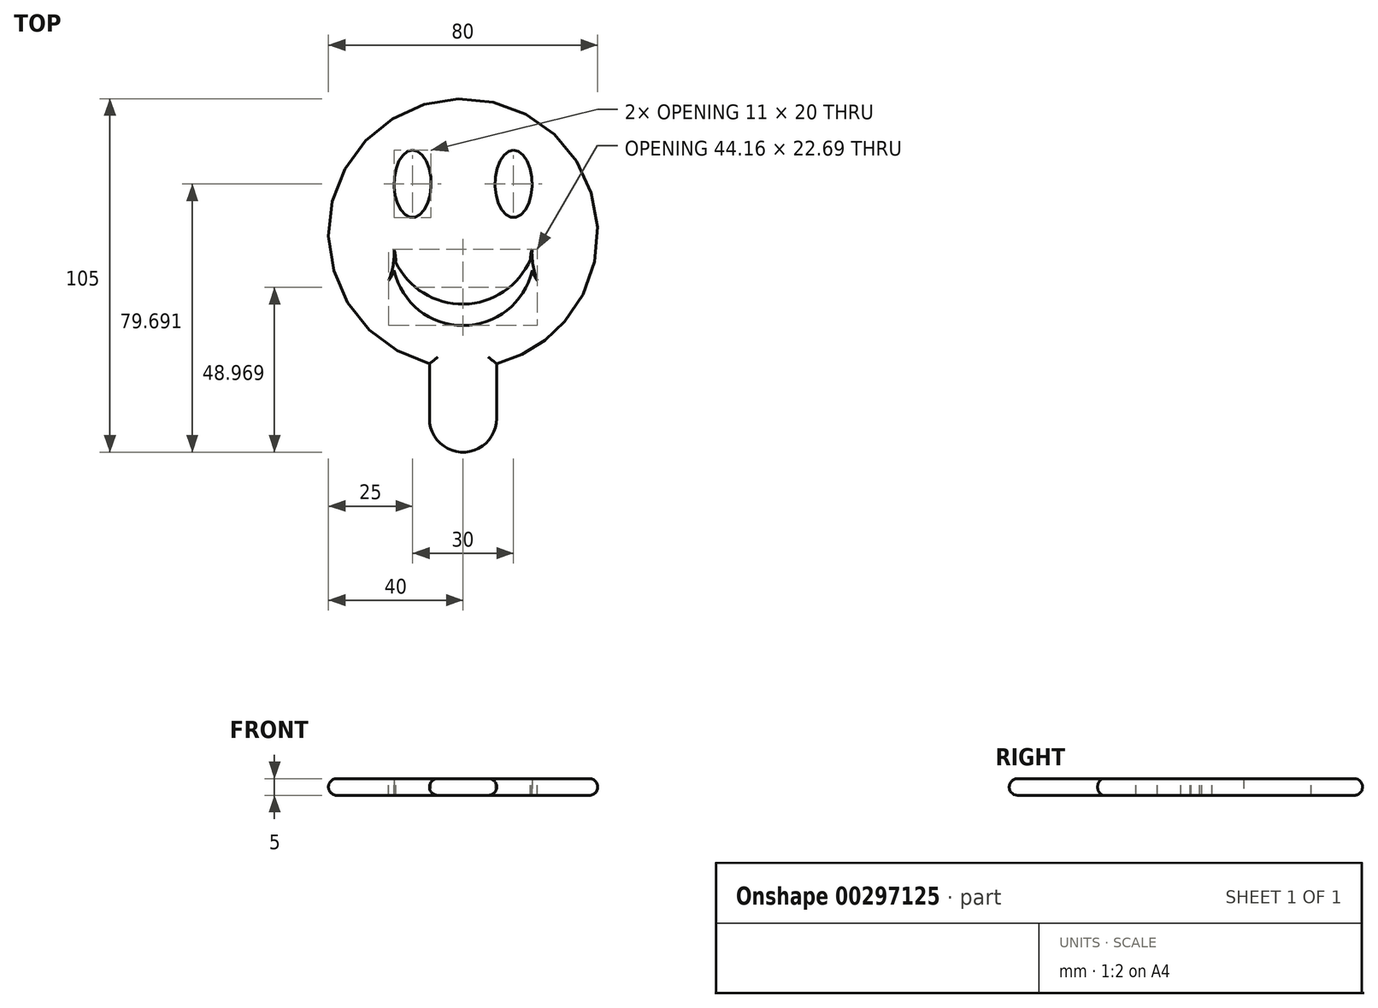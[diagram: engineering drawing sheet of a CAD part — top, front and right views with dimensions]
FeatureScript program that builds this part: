
annotation { "Feature Type Name" : "Feature", "Feature Type Description" : "" }
export const myFeature = defineFeature(function(context is Context, id is Id, definition is map)
    precondition{}
    {
        {
            var Q0;
            Q0=qCreatedBy(makeId("Top.planeOp"),FACE);
            var sketch = newSketch(context, id + "F0", { "sketchPlane" : qUnion([Q0])});
            skCircle(sketch, "E0", {"center": v(0, 0) * mm, "radius": 40 * mm});
            skText(sketch, "E1", { "text": "JODIE", "fontName": "AllertaStencil-Regular.ttf"});
            const initialGuessF0  = {"E1": [-0.0273, -0.00648, 1, 0, 0.0135]};
            skSetInitialGuess(sketch, initialGuessF0);
            skSolve(sketch);
        }
        {
            var Q0;
            Q0=qSketchRegion(id+"F0",true);
            extrude(context, id + "F1", {"entities" : qUnion([Q0]), "depth" : 5 * mm});
        }
        {
            var Q0;
            Q0=qCreatedBy(makeId("Top.planeOp"),FACE);
            var sketch = newSketch(context, id + "F2", { "sketchPlane" : qUnion([Q0])});
            skLineSegment(sketch, "E2.bottom", {"start": v(-10, -65) * mm, "end": v(10, -65) * mm});
            skLineSegment(sketch, "E2.top", {"start": v(-10, 65) * mm, "end": v(10, 65) * mm});
            skLineSegment(sketch, "E2.left", {"start": v(-10, -65) * mm, "end": v(-10, 65) * mm});
            skLineSegment(sketch, "E2.right", {"start": v(10, -65) * mm, "end": v(10, 65) * mm});
            skPoint(sketch, "E2.middle", {"position": v(0, 0) * mm});
            skLineSegment(sketch, "E3", {"start": v(-10, -31.18) * mm, "end": v(10, -31.18) * mm});
            skSolve(sketch);
        }
        {
            var Q0;
            {var subQ0=sQuery(id+"F2.wireOp",EDGE,"E2.bottom");Q0=makeQuery(id+"F2.imprint","IMPRINT",FACE,{"disambiguationData":[TD([[makeQuery(id+"F2.imprint","IMPRINT",EDGE,{"derivedFrom":subQ0}),1.0]])]});}
            extrude(context, id + "F3", {"entities" : qUnion([Q0]), "operationType" : NewBodyOperationType.ADD, "depth" : 5 * mm});
        }
        {
            var Q0;
            Q0=makeQuery(id+"F3.opExtrude","SWEPT_EDGE",EDGE,{"disambiguationData":[OSD([sQuery(id+"F2.wireOp",EDGE,"E2.bottom"),sQuery(id+"F2.wireOp",EDGE,"E2.left")])]});
            var Q1;
            Q1=makeQuery(id+"F3.opExtrude","SWEPT_EDGE",EDGE,{"disambiguationData":[OSD([sQuery(id+"F2.wireOp",EDGE,"E2.bottom"),sQuery(id+"F2.wireOp",EDGE,"E2.right")])]});
            fillet(context, id + "F4", {"entities" : qUnion([Q0, Q1]), "radius" : 10 * mm, "tangentPropagation" : true, "allowEdgeOverflow" : false});
        }
        {
            var Q0;
            Q0=makeQuery(id+"F1.opExtrude","CAP_EDGE",EDGE,{"disambiguationData":[OSD([sQuery(id+"F0.wireOp",EDGE,"E0")])],"isStart":false});
            var Q1;
            Q1=makeQuery(id+"F3.opExtrude","CAP_EDGE",EDGE,{"disambiguationData":[OSD([sQuery(id+"F2.wireOp",EDGE,"E2.left")])],"isStart":false});
            fillet(context, id + "F5", {"entities" : qUnion([Q0, Q1]), "radius" : 2.5 * mm, "tangentPropagation" : true, "allowEdgeOverflow" : false});
        }
        {
            var Q0;
            Q0=makeQuery(id+"F1.opExtrude","CAP_EDGE",EDGE,{"disambiguationData":[OSD([sQuery(id+"F0.wireOp",EDGE,"E0")])],"isStart":true});
            var Q1;
            Q1=makeQuery(id+"F3.opExtrude","CAP_EDGE",EDGE,{"disambiguationData":[OSD([sQuery(id+"F2.wireOp",EDGE,"E2.left")])],"isStart":true});
            fillet(context, id + "F6", {"entities" : qUnion([Q0, Q1]), "radius" : 2.5 * mm, "tangentPropagation" : true, "allowEdgeOverflow" : false});
        }
        {
            var Q0;
            Q0=makeQuery(id+"F3.boolean.opBoolean","MERGE",FACE,{"derivedFrom":[makeQuery(id+"F1.opExtrude","CAP_FACE",FACE,{"disambiguationData":[OSD([sQuery(id+"F0.wireOp",EDGE,"E0"),sQuery(id+"F0.wireOp",EDGE,"E1.sketch_text.stroke-0"),sQuery(id+"F0.wireOp",EDGE,"E1.sketch_text.stroke-1"),sQuery(id+"F0.wireOp",EDGE,"E1.sketch_text.stroke-2"),sQuery(id+"F0.wireOp",EDGE,"E1.sketch_text.stroke-3"),sQuery(id+"F0.wireOp",EDGE,"E1.sketch_text.stroke-4"),sQuery(id+"F0.wireOp",EDGE,"E1.sketch_text.stroke-5"),sQuery(id+"F0.wireOp",EDGE,"E1.sketch_text.stroke-6"),sQuery(id+"F0.wireOp",EDGE,"E1.sketch_text.stroke-7"),sQuery(id+"F0.wireOp",EDGE,"E1.sketch_text.stroke-8"),sQuery(id+"F0.wireOp",EDGE,"E1.sketch_text.stroke-9"),sQuery(id+"F0.wireOp",EDGE,"E1.sketch_text.stroke-10"),sQuery(id+"F0.wireOp",EDGE,"E1.sketch_text.stroke-11"),sQuery(id+"F0.wireOp",EDGE,"E1.sketch_text.stroke-12"),sQuery(id+"F0.wireOp",EDGE,"E1.sketch_text.stroke-13"),sQuery(id+"F0.wireOp",EDGE,"E1.sketch_text.stroke-14"),sQuery(id+"F0.wireOp",EDGE,"E1.sketch_text.stroke-15"),sQuery(id+"F0.wireOp",EDGE,"E1.sketch_text.stroke-16"),sQuery(id+"F0.wireOp",EDGE,"E1.sketch_text.stroke-17"),sQuery(id+"F0.wireOp",EDGE,"E1.sketch_text.stroke-18"),sQuery(id+"F0.wireOp",EDGE,"E1.sketch_text.stroke-19"),sQuery(id+"F0.wireOp",EDGE,"E1.sketch_text.stroke-20"),sQuery(id+"F0.wireOp",EDGE,"E1.sketch_text.stroke-21"),sQuery(id+"F0.wireOp",EDGE,"E1.sketch_text.stroke-22"),sQuery(id+"F0.wireOp",EDGE,"E1.sketch_text.stroke-23"),sQuery(id+"F0.wireOp",EDGE,"E1.sketch_text.stroke-24"),sQuery(id+"F0.wireOp",EDGE,"E1.sketch_text.stroke-25"),sQuery(id+"F0.wireOp",EDGE,"E1.sketch_text.stroke-26"),sQuery(id+"F0.wireOp",EDGE,"E1.sketch_text.stroke-27"),sQuery(id+"F0.wireOp",EDGE,"E1.sketch_text.stroke-28"),sQuery(id+"F0.wireOp",EDGE,"E1.sketch_text.stroke-29"),sQuery(id+"F0.wireOp",EDGE,"E1.sketch_text.stroke-30"),sQuery(id+"F0.wireOp",EDGE,"E1.sketch_text.stroke-31"),sQuery(id+"F0.wireOp",EDGE,"E1.sketch_text.stroke-32"),sQuery(id+"F0.wireOp",EDGE,"E1.sketch_text.stroke-33"),sQuery(id+"F0.wireOp",EDGE,"E1.sketch_text.stroke-34"),sQuery(id+"F0.wireOp",EDGE,"E1.sketch_text.stroke-35"),sQuery(id+"F0.wireOp",EDGE,"E1.sketch_text.stroke-36"),sQuery(id+"F0.wireOp",EDGE,"E1.sketch_text.stroke-37"),sQuery(id+"F0.wireOp",EDGE,"E1.sketch_text.stroke-38"),sQuery(id+"F0.wireOp",EDGE,"E1.sketch_text.stroke-39"),sQuery(id+"F0.wireOp",EDGE,"E1.sketch_text.stroke-40"),sQuery(id+"F0.wireOp",EDGE,"E1.sketch_text.stroke-41"),sQuery(id+"F0.wireOp",EDGE,"E1.sketch_text.stroke-42"),sQuery(id+"F0.wireOp",EDGE,"E1.sketch_text.stroke-43"),sQuery(id+"F0.wireOp",EDGE,"E1.sketch_text.stroke-44"),sQuery(id+"F0.wireOp",EDGE,"E1.sketch_text.stroke-45"),sQuery(id+"F0.wireOp",EDGE,"E1.sketch_text.stroke-46"),sQuery(id+"F0.wireOp",EDGE,"E1.sketch_text.stroke-47"),sQuery(id+"F0.wireOp",EDGE,"E1.sketch_text.stroke-48"),sQuery(id+"F0.wireOp",EDGE,"E1.sketch_text.stroke-49"),sQuery(id+"F0.wireOp",EDGE,"E1.sketch_text.stroke-50"),sQuery(id+"F0.wireOp",EDGE,"E1.sketch_text.stroke-51"),sQuery(id+"F0.wireOp",EDGE,"E1.sketch_text.stroke-52"),sQuery(id+"F0.wireOp",EDGE,"E1.sketch_text.stroke-53"),sQuery(id+"F0.wireOp",EDGE,"E1.sketch_text.stroke-54"),sQuery(id+"F0.wireOp",EDGE,"E1.sketch_text.stroke-55"),sQuery(id+"F0.wireOp",EDGE,"E1.sketch_text.stroke-56"),sQuery(id+"F0.wireOp",EDGE,"E1.sketch_text.stroke-57"),sQuery(id+"F0.wireOp",EDGE,"E1.sketch_text.stroke-58"),sQuery(id+"F0.wireOp",EDGE,"E1.sketch_text.stroke-59"),sQuery(id+"F0.wireOp",EDGE,"E1.sketch_text.stroke-60"),sQuery(id+"F0.wireOp",EDGE,"E1.sketch_text.stroke-61"),sQuery(id+"F0.wireOp",EDGE,"E1.sketch_text.stroke-62"),sQuery(id+"F0.wireOp",EDGE,"E1.sketch_text.stroke-63"),sQuery(id+"F0.wireOp",EDGE,"E1.sketch_text.stroke-64"),sQuery(id+"F0.wireOp",EDGE,"E1.sketch_text.stroke-65"),sQuery(id+"F0.wireOp",EDGE,"E1.sketch_text.stroke-66"),sQuery(id+"F0.wireOp",EDGE,"E1.sketch_text.stroke-67"),sQuery(id+"F0.wireOp",EDGE,"E1.sketch_text.stroke-68"),sQuery(id+"F0.wireOp",EDGE,"E1.sketch_text.stroke-69"),sQuery(id+"F0.wireOp",EDGE,"E1.sketch_text.stroke-70"),sQuery(id+"F0.wireOp",EDGE,"E1.sketch_text.stroke-71"),sQuery(id+"F0.wireOp",EDGE,"E1.sketch_text.stroke-72"),sQuery(id+"F0.wireOp",EDGE,"E1.sketch_text.stroke-73"),sQuery(id+"F0.wireOp",EDGE,"E1.sketch_text.stroke-74"),sQuery(id+"F0.wireOp",EDGE,"E1.sketch_text.stroke-75"),sQuery(id+"F0.wireOp",EDGE,"E1.sketch_text.stroke-76"),sQuery(id+"F0.wireOp",EDGE,"E1.sketch_text.stroke-77"),sQuery(id+"F0.wireOp",EDGE,"E1.sketch_text.stroke-78"),sQuery(id+"F0.wireOp",EDGE,"E1.sketch_text.stroke-79"),sQuery(id+"F0.wireOp",EDGE,"E1.sketch_text.stroke-80"),sQuery(id+"F0.wireOp",EDGE,"E1.sketch_text.stroke-81"),sQuery(id+"F0.wireOp",EDGE,"E1.sketch_text.stroke-82"),sQuery(id+"F0.wireOp",EDGE,"E1.sketch_text.stroke-83"),sQuery(id+"F0.wireOp",EDGE,"E1.sketch_text.stroke-84"),sQuery(id+"F0.wireOp",EDGE,"E1.sketch_text.stroke-85"),sQuery(id+"F0.wireOp",EDGE,"E1.sketch_text.stroke-86"),sQuery(id+"F0.wireOp",EDGE,"E1.sketch_text.stroke-87"),sQuery(id+"F0.wireOp",EDGE,"E1.sketch_text.stroke-88"),sQuery(id+"F0.wireOp",EDGE,"E1.sketch_text.stroke-89"),sQuery(id+"F0.wireOp",EDGE,"E1.sketch_text.stroke-90"),sQuery(id+"F0.wireOp",EDGE,"E1.sketch_text.stroke-91"),sQuery(id+"F0.wireOp",EDGE,"E1.sketch_text.stroke-92"),sQuery(id+"F0.wireOp",EDGE,"E1.sketch_text.stroke-93"),sQuery(id+"F0.wireOp",EDGE,"E1.sketch_text.stroke-94"),sQuery(id+"F0.wireOp",EDGE,"E1.sketch_text.stroke-95"),sQuery(id+"F0.wireOp",EDGE,"E1.sketch_text.stroke-96"),sQuery(id+"F0.wireOp",EDGE,"E1.sketch_text.stroke-97"),sQuery(id+"F0.wireOp",EDGE,"E1.sketch_text.stroke-98"),sQuery(id+"F0.wireOp",EDGE,"E1.sketch_text.stroke-99")])],"isStart":false}),makeQuery(id+"F3.opExtrude","CAP_FACE",FACE,{"disambiguationData":[OSD([sQuery(id+"F2.wireOp",EDGE,"E2.bottom"),sQuery(id+"F2.wireOp",EDGE,"E2.left"),sQuery(id+"F2.wireOp",EDGE,"E2.right"),sQuery(id+"F2.wireOp",EDGE,"E3")])],"isStart":false})]});
            var sketch = newSketch(context, id + "F7", { "sketchPlane" : qUnion([Q0])});
            skLineSegment(sketch, "E4.bottom", {"start": v(-29.13, 16.78) * mm, "end": v(29.1, 16.78) * mm});
            skLineSegment(sketch, "E4.top", {"start": v(-29.13, -17.75) * mm, "end": v(29.1, -17.75) * mm});
            skLineSegment(sketch, "E4.left", {"start": v(-29.13, 16.78) * mm, "end": v(-29.13, -17.75) * mm});
            skLineSegment(sketch, "E4.right", {"start": v(29.1, 16.78) * mm, "end": v(29.1, -17.75) * mm});
            skSolve(sketch);
        }
        {
            var Q0;
            Q0 = qSketchRegion(id + "F7", true);
            extrude(context, id + "F8", {"entities" : qUnion([Q0]), "operationType" : NewBodyOperationType.ADD, "oppositeDirection" : true, "depth" : 5 * mm});
        }
        {
            var Q0;
            Q0=makeQuery(id+"F8.boolean.opBoolean","MERGE",FACE,{"derivedFrom":[makeQuery(id+"F3.boolean.opBoolean","MERGE",FACE,{"derivedFrom":[makeQuery(id+"F1.opExtrude","CAP_FACE",FACE,{"disambiguationData":[OSD([sQuery(id+"F0.wireOp",EDGE,"E0"),sQuery(id+"F0.wireOp",EDGE,"E1.sketch_text.stroke-0"),sQuery(id+"F0.wireOp",EDGE,"E1.sketch_text.stroke-1"),sQuery(id+"F0.wireOp",EDGE,"E1.sketch_text.stroke-2"),sQuery(id+"F0.wireOp",EDGE,"E1.sketch_text.stroke-3"),sQuery(id+"F0.wireOp",EDGE,"E1.sketch_text.stroke-4"),sQuery(id+"F0.wireOp",EDGE,"E1.sketch_text.stroke-5"),sQuery(id+"F0.wireOp",EDGE,"E1.sketch_text.stroke-6"),sQuery(id+"F0.wireOp",EDGE,"E1.sketch_text.stroke-7"),sQuery(id+"F0.wireOp",EDGE,"E1.sketch_text.stroke-8"),sQuery(id+"F0.wireOp",EDGE,"E1.sketch_text.stroke-9"),sQuery(id+"F0.wireOp",EDGE,"E1.sketch_text.stroke-10"),sQuery(id+"F0.wireOp",EDGE,"E1.sketch_text.stroke-11"),sQuery(id+"F0.wireOp",EDGE,"E1.sketch_text.stroke-12"),sQuery(id+"F0.wireOp",EDGE,"E1.sketch_text.stroke-13"),sQuery(id+"F0.wireOp",EDGE,"E1.sketch_text.stroke-14"),sQuery(id+"F0.wireOp",EDGE,"E1.sketch_text.stroke-15"),sQuery(id+"F0.wireOp",EDGE,"E1.sketch_text.stroke-16"),sQuery(id+"F0.wireOp",EDGE,"E1.sketch_text.stroke-17"),sQuery(id+"F0.wireOp",EDGE,"E1.sketch_text.stroke-18"),sQuery(id+"F0.wireOp",EDGE,"E1.sketch_text.stroke-19"),sQuery(id+"F0.wireOp",EDGE,"E1.sketch_text.stroke-20"),sQuery(id+"F0.wireOp",EDGE,"E1.sketch_text.stroke-21"),sQuery(id+"F0.wireOp",EDGE,"E1.sketch_text.stroke-22"),sQuery(id+"F0.wireOp",EDGE,"E1.sketch_text.stroke-23"),sQuery(id+"F0.wireOp",EDGE,"E1.sketch_text.stroke-24"),sQuery(id+"F0.wireOp",EDGE,"E1.sketch_text.stroke-25"),sQuery(id+"F0.wireOp",EDGE,"E1.sketch_text.stroke-26"),sQuery(id+"F0.wireOp",EDGE,"E1.sketch_text.stroke-27"),sQuery(id+"F0.wireOp",EDGE,"E1.sketch_text.stroke-28"),sQuery(id+"F0.wireOp",EDGE,"E1.sketch_text.stroke-29"),sQuery(id+"F0.wireOp",EDGE,"E1.sketch_text.stroke-30"),sQuery(id+"F0.wireOp",EDGE,"E1.sketch_text.stroke-31"),sQuery(id+"F0.wireOp",EDGE,"E1.sketch_text.stroke-32"),sQuery(id+"F0.wireOp",EDGE,"E1.sketch_text.stroke-33"),sQuery(id+"F0.wireOp",EDGE,"E1.sketch_text.stroke-34"),sQuery(id+"F0.wireOp",EDGE,"E1.sketch_text.stroke-35"),sQuery(id+"F0.wireOp",EDGE,"E1.sketch_text.stroke-36"),sQuery(id+"F0.wireOp",EDGE,"E1.sketch_text.stroke-37"),sQuery(id+"F0.wireOp",EDGE,"E1.sketch_text.stroke-38"),sQuery(id+"F0.wireOp",EDGE,"E1.sketch_text.stroke-39"),sQuery(id+"F0.wireOp",EDGE,"E1.sketch_text.stroke-40"),sQuery(id+"F0.wireOp",EDGE,"E1.sketch_text.stroke-41"),sQuery(id+"F0.wireOp",EDGE,"E1.sketch_text.stroke-42"),sQuery(id+"F0.wireOp",EDGE,"E1.sketch_text.stroke-43"),sQuery(id+"F0.wireOp",EDGE,"E1.sketch_text.stroke-44"),sQuery(id+"F0.wireOp",EDGE,"E1.sketch_text.stroke-45"),sQuery(id+"F0.wireOp",EDGE,"E1.sketch_text.stroke-46"),sQuery(id+"F0.wireOp",EDGE,"E1.sketch_text.stroke-47"),sQuery(id+"F0.wireOp",EDGE,"E1.sketch_text.stroke-48"),sQuery(id+"F0.wireOp",EDGE,"E1.sketch_text.stroke-49"),sQuery(id+"F0.wireOp",EDGE,"E1.sketch_text.stroke-50"),sQuery(id+"F0.wireOp",EDGE,"E1.sketch_text.stroke-51"),sQuery(id+"F0.wireOp",EDGE,"E1.sketch_text.stroke-52"),sQuery(id+"F0.wireOp",EDGE,"E1.sketch_text.stroke-53"),sQuery(id+"F0.wireOp",EDGE,"E1.sketch_text.stroke-54"),sQuery(id+"F0.wireOp",EDGE,"E1.sketch_text.stroke-55"),sQuery(id+"F0.wireOp",EDGE,"E1.sketch_text.stroke-56"),sQuery(id+"F0.wireOp",EDGE,"E1.sketch_text.stroke-57"),sQuery(id+"F0.wireOp",EDGE,"E1.sketch_text.stroke-58"),sQuery(id+"F0.wireOp",EDGE,"E1.sketch_text.stroke-59"),sQuery(id+"F0.wireOp",EDGE,"E1.sketch_text.stroke-60"),sQuery(id+"F0.wireOp",EDGE,"E1.sketch_text.stroke-61"),sQuery(id+"F0.wireOp",EDGE,"E1.sketch_text.stroke-62"),sQuery(id+"F0.wireOp",EDGE,"E1.sketch_text.stroke-63"),sQuery(id+"F0.wireOp",EDGE,"E1.sketch_text.stroke-64"),sQuery(id+"F0.wireOp",EDGE,"E1.sketch_text.stroke-65"),sQuery(id+"F0.wireOp",EDGE,"E1.sketch_text.stroke-66"),sQuery(id+"F0.wireOp",EDGE,"E1.sketch_text.stroke-67"),sQuery(id+"F0.wireOp",EDGE,"E1.sketch_text.stroke-68"),sQuery(id+"F0.wireOp",EDGE,"E1.sketch_text.stroke-69"),sQuery(id+"F0.wireOp",EDGE,"E1.sketch_text.stroke-70"),sQuery(id+"F0.wireOp",EDGE,"E1.sketch_text.stroke-71"),sQuery(id+"F0.wireOp",EDGE,"E1.sketch_text.stroke-72"),sQuery(id+"F0.wireOp",EDGE,"E1.sketch_text.stroke-73"),sQuery(id+"F0.wireOp",EDGE,"E1.sketch_text.stroke-74"),sQuery(id+"F0.wireOp",EDGE,"E1.sketch_text.stroke-75"),sQuery(id+"F0.wireOp",EDGE,"E1.sketch_text.stroke-76"),sQuery(id+"F0.wireOp",EDGE,"E1.sketch_text.stroke-77"),sQuery(id+"F0.wireOp",EDGE,"E1.sketch_text.stroke-78"),sQuery(id+"F0.wireOp",EDGE,"E1.sketch_text.stroke-79"),sQuery(id+"F0.wireOp",EDGE,"E1.sketch_text.stroke-80"),sQuery(id+"F0.wireOp",EDGE,"E1.sketch_text.stroke-81"),sQuery(id+"F0.wireOp",EDGE,"E1.sketch_text.stroke-82"),sQuery(id+"F0.wireOp",EDGE,"E1.sketch_text.stroke-83"),sQuery(id+"F0.wireOp",EDGE,"E1.sketch_text.stroke-84"),sQuery(id+"F0.wireOp",EDGE,"E1.sketch_text.stroke-85"),sQuery(id+"F0.wireOp",EDGE,"E1.sketch_text.stroke-86"),sQuery(id+"F0.wireOp",EDGE,"E1.sketch_text.stroke-87"),sQuery(id+"F0.wireOp",EDGE,"E1.sketch_text.stroke-88"),sQuery(id+"F0.wireOp",EDGE,"E1.sketch_text.stroke-89"),sQuery(id+"F0.wireOp",EDGE,"E1.sketch_text.stroke-90"),sQuery(id+"F0.wireOp",EDGE,"E1.sketch_text.stroke-91"),sQuery(id+"F0.wireOp",EDGE,"E1.sketch_text.stroke-92"),sQuery(id+"F0.wireOp",EDGE,"E1.sketch_text.stroke-93"),sQuery(id+"F0.wireOp",EDGE,"E1.sketch_text.stroke-94"),sQuery(id+"F0.wireOp",EDGE,"E1.sketch_text.stroke-95"),sQuery(id+"F0.wireOp",EDGE,"E1.sketch_text.stroke-96"),sQuery(id+"F0.wireOp",EDGE,"E1.sketch_text.stroke-97"),sQuery(id+"F0.wireOp",EDGE,"E1.sketch_text.stroke-98"),sQuery(id+"F0.wireOp",EDGE,"E1.sketch_text.stroke-99")])],"isStart":false}),makeQuery(id+"F3.opExtrude","CAP_FACE",FACE,{"disambiguationData":[OSD([sQuery(id+"F2.wireOp",EDGE,"E2.bottom"),sQuery(id+"F2.wireOp",EDGE,"E2.left"),sQuery(id+"F2.wireOp",EDGE,"E2.right"),sQuery(id+"F2.wireOp",EDGE,"E3")])],"isStart":false})]}),makeQuery(id+"F8.opExtrude","CAP_FACE",FACE,{"disambiguationData":[OSD([sQuery(id+"F7.wireOp",EDGE,"E4.bottom"),sQuery(id+"F7.wireOp",EDGE,"E4.top"),sQuery(id+"F7.wireOp",EDGE,"E4.left"),sQuery(id+"F7.wireOp",EDGE,"E4.right")])],"isStart":true})]});
            var sketch = newSketch(context, id + "F9", { "sketchPlane" : qUnion([Q0])});
            skLineSegment(sketch, "E5", {"start": v(0, 0) * mm, "end": v(0, 38.3) * mm});
            skLineSegment(sketch, "E6", {"start": v(0, 38.3) * mm, "end": v(0, -56.22) * mm, "construction": true});
            skLineSegment(sketch, "E7", {"start": v(40.12, 0) * mm, "end": v(-35.55, 0) * mm, "construction": true});
            skLineSegment(sketch, "E8", {"start": v(0, 19.15) * mm, "end": v(-15, 19.15) * mm, "construction": true});
            skPoint(sketch, "E8.endSnap0", {"position": v(0, 19.15) * mm});
            skLineSegment(sketch, "E9", {"start": v(-15, 19.15) * mm, "end": v(0, 19.15) * mm, "construction": true});
            skLineSegment(sketch, "E10", {"start": v(15, 19.15) * mm, "end": v(0, 19.15) * mm, "construction": true});
            skEllipse(sketch, "E11", {"center": v(-15, 14.7) * mm, "majorRadius": 10 * mm, "minorRadius": 5.5 * mm, "majorAxis": v(0, 1)});
            skEllipse(sketch, "E12", {"center": v(15, 14.7) * mm, "majorRadius": 10 * mm, "minorRadius": 5.5 * mm, "majorAxis": v(0, 1)});
            skPoint(sketch, "E12.centerSnap0", {"position": v(-9.5, 14.7) * mm});
            skLineSegment(sketch, "E13", {"start": v(-20.5, 14.7) * mm, "end": v(-20.5, -26.66) * mm, "construction": true});
            skLineSegment(sketch, "E14", {"start": v(20.5, 14.7) * mm, "end": v(20.5, -27.72) * mm, "construction": true});
            skArc(sketch, "E15", {"start": v(-20.04, -8.44) * mm, "mid": v(0.22, -21.02) * mm, "end": v(20.02, -7.72) * mm});
            skArc(sketch, "E16", {"start": v(-20.5, -11.15) * mm, "mid": v(0, -27.38) * mm, "end": v(20.5, -11.15) * mm});
            skArc(sketch, "E17", {"start": v(-22.08, -14) * mm, "mid": v(-21.16, -12.53) * mm, "end": v(-20.5, -10.91) * mm});
            skArc(sketch, "E18.MirrorCS", {"start": v(22.08, -14) * mm, "mid": v(21.16, -12.53) * mm, "end": v(20.5, -10.91) * mm});
            skArc(sketch, "E19", {"start": v(-22.08, -14) * mm, "mid": v(-20.79, -9.43) * mm, "end": v(-20.5, -4.69) * mm});
            skArc(sketch, "E20.MirrorCS", {"start": v(22.08, -14) * mm, "mid": v(20.79, -9.43) * mm, "end": v(20.5, -4.69) * mm});
            skArc(sketch, "E21.trimOffspring", {"start": v(-20.04, -8.44) * mm, "mid": v(-20.1, -6.54) * mm, "end": v(-20.5, -4.69) * mm});
            skArc(sketch, "E22.trimOffspring", {"start": v(20.02, -7.72) * mm, "mid": v(20.15, -6.19) * mm, "end": v(20.5, -4.69) * mm});
            skArc(sketch, "E23.trimOffspring", {"start": v(20.5, -6.54) * mm, "mid": v(20.5, -6.53) * mm, "end": v(20.5, -6.52) * mm});
            skLineSegment(sketch, "E24", {"start": v(-20.5, -11.15) * mm, "end": v(-20.5, -10.91) * mm});
            skLineSegment(sketch, "E25", {"start": v(20.5, -11.15) * mm, "end": v(20.5, -10.91) * mm});
            skSolve(sketch);
        }
        {
            var Q0;
            Q0 = qSketchRegion(id + "F9", true);
            extrude(context, id + "F10", {"entities" : qUnion([Q0]), "operationType" : NewBodyOperationType.REMOVE, "oppositeDirection" : true, "depth" : 25 * mm});
        }
    });
